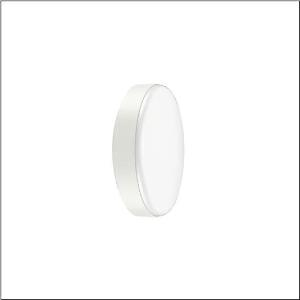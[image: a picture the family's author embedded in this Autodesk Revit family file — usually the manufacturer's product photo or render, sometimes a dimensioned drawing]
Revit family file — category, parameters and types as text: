
# Revit family: rondel_31_51wc10ma32a
name_source: partatom
category: Lighting Fixtures
units: mm (PartAtom-declared; Revit-internal decimal feet)

## family parameters
Cut with Voids When Loaded = No
Host = Face
Light Source = No
Part Type = Normal
Room Calculation Point = No
Round Connector Dimension = Use Diameter
Shared = No

## types (1)
- --- (1 x LED, 2450 lm, 19 W, 3000K)
    Apparent Load = 19 VA
    CIE Flux Codes = 44 75 94 94 100
    Color Rendering = 80
    Color Temperature = 3000K
    Default Elevation = 1800 mm
    Description = Rondel 31, wall and ceiling luminaire, primary optical cover: cover, of PC, opal, light emission: direct distribution, primary light characteristic: symmetric, installation type: surface-mounted, LED, rated luminous flux: 2.450lm, luminous efficacy: 129lm/W, light colour: 830, colour temperature: 3000K, with terminal, 3-pole, max. 2.5mm², mains connection: 220..240V, AC, 50/60Hz, rated input power: 19W, luminaire housing, of PC, traffic white (RAL 9016), diameter: 350mm, protection rating (complete): IP65, insulation class (complete): insulation class II (safety insulation), certification: CE, impact resistance: IK10, permissible operating ambient temperature: -20..+40°C, permissible storage temperature: -20..+60°C, packaging unit: 1 piece
    Height = 97 mm
    Lamp = 1 x LED
    Lamp Light Flux = 2450 lm
    Lamp Power = 19 W
    Lamp count = 1
    Length = 350 mm
    Luminous efficacy = 129 lm/W
    Manufacturer = Siteco
    ModVariant = No
    Model = 51WC10MA32A
    Mounting Place = Ceiling
    Mounting Type = Surface mounted
    Number of Poles = 1
    OnlyDefault = Yes
    Power Factor = 1
    Product Name = Rondel 31
    Product group = wall and ceiling luminaire
    ProductGroupID = 302
    Protection Class = Protection class II
    Protection Degree = IP 65
    RLX_Detail_Level = 1
    RLX_Emergency_Light_Flux = 0 lm
    RLX_Emergency_Type = 0
    RLX_Emergency_Type_DB = No
    RlxData = <blob elided: 30013 chars, md5=e9d7a79d>
    Socket = socket
    Standby Power = 0 W
    System Light Flux = 2450 lm
    System Power = 19 W
    Type Comments = factory setting: luminous flux: 100 % | (ON | ON)
    Type Image = l_1007027.jpg
    URL = http://relux.com
    VarID = @adj_101029
    Voltage = 0 V
    Weight = 0.00 kg
    Width = 0 mm  [stored 0 ft]

note: [stored X ft] marks values corroborated as IEEE doubles in the binary element streams (Revit-internal decimal feet)

## geometry (parser evidence)
native form markers: Blend x4, Sweep x11
no freeform markers — native parametric forms only
